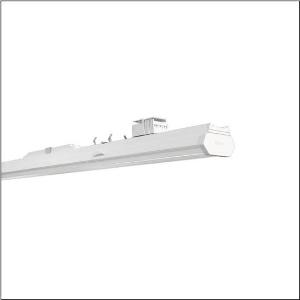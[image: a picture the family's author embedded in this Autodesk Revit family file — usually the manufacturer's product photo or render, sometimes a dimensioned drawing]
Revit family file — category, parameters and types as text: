
# Revit family: licross_r__11_protected_ho_51td11mn4gxs_4279
name_source: partatom
category: Lighting Fixtures
units: mm (PartAtom-declared; Revit-internal decimal feet)

## family parameters
Cut with Voids When Loaded = No
Host = Face
Light Source = No
Part Type = Normal
Room Calculation Point = No
Round Connector Dimension = Use Diameter
Shared = No

## types (1)
- --- (1 x LED, 16070 lm, 87.4 W, 4000K)
    Apparent Load = 87 VA
    CIE Flux Codes = 84 94 98 99 100
    Color Rendering = 80
    Color Temperature = 4000K
    Default Elevation = 1800 mm
    Description = Licross® 11 Protected HO, luminaire insert, of sheet steel, galvanised, coil coated, white, length: 1.500mm, width: 90mm, height: 101mm, LED rated luminous flux: 16.070lm, light colour: 840, control gear: ON/OFF Multilumen, with plug, 3-pole, with phase selection, mains connection: 220..240V, AC, 50/60Hz, rated input power: 87W, halogen-free wiring, primary light control with lens, of plastic, primary optical cover: cover, of PMMA, light emission: direct distribution, primary light characteristic: symmetric, protection rating (complete): IP54, insulation class (complete): insulation class I (protective earthing), certification: CE, ENEC, VDE, UKCA, protection symbol: D if used in an environment with non-conductive dust loads with corresponding accessories, impact resistance: IK06, permissible ambient temperature for indoor applications: -35..+35°C, corresponds to IFS (International Featured Standards) requirements for safety and quality in the food industry, reducing of maximum allowable ambient temperature of 5°C with ceiling mounting, LABS conformity tested according to VDMA 24364:2018-05, packaging unit: 1 piece
    Height = 92 mm
    Lamp = 1 x LED
    Lamp Light Flux = 16070 lm
    Lamp Power = 87.4 W
    Lamp count = 1
    Length = 1500 mm
    Luminous efficacy = 184 lm/W
    Manufacturer = Siteco
    ModVariant = No
    Model = 51TD11MN4GXS
    Mounting Place = Ceiling
    Mounting Type = Pendant
    Number of Poles = 1
    OnlyDefault = Yes
    Power Factor = 1
    Product Name = Licross® 11 Protected HO
    Product group = luminaire insert
    ProductGroupID = 901
    Protection Class = Protection class I
    Protection Degree = IP 54
    RLX_Detail_Level = 1
    RLX_Emergency_Light_Flux = 0 lm
    RLX_Emergency_Type = 0
    RLX_Emergency_Type_DB = No
    RlxData = <blob elided: 22089 chars, md5=94352648>
    Socket = socket
    Standby Power = 0 W
    System Light Flux = 16070 lm
    System Power = 87 W
    Type Comments = factory setting: luminous flux: 100 % | (A | C | E) | 203 mA
    Type Image = l_1256145.jpg
    URL = http://relux.com
    VarID = @adj_019379
    Voltage = 0 V
    Weight = 0.00 kg
    Width = 88 mm

## geometry (parser evidence)
native form markers: Blend x4, Sweep x13
no freeform markers — native parametric forms only
